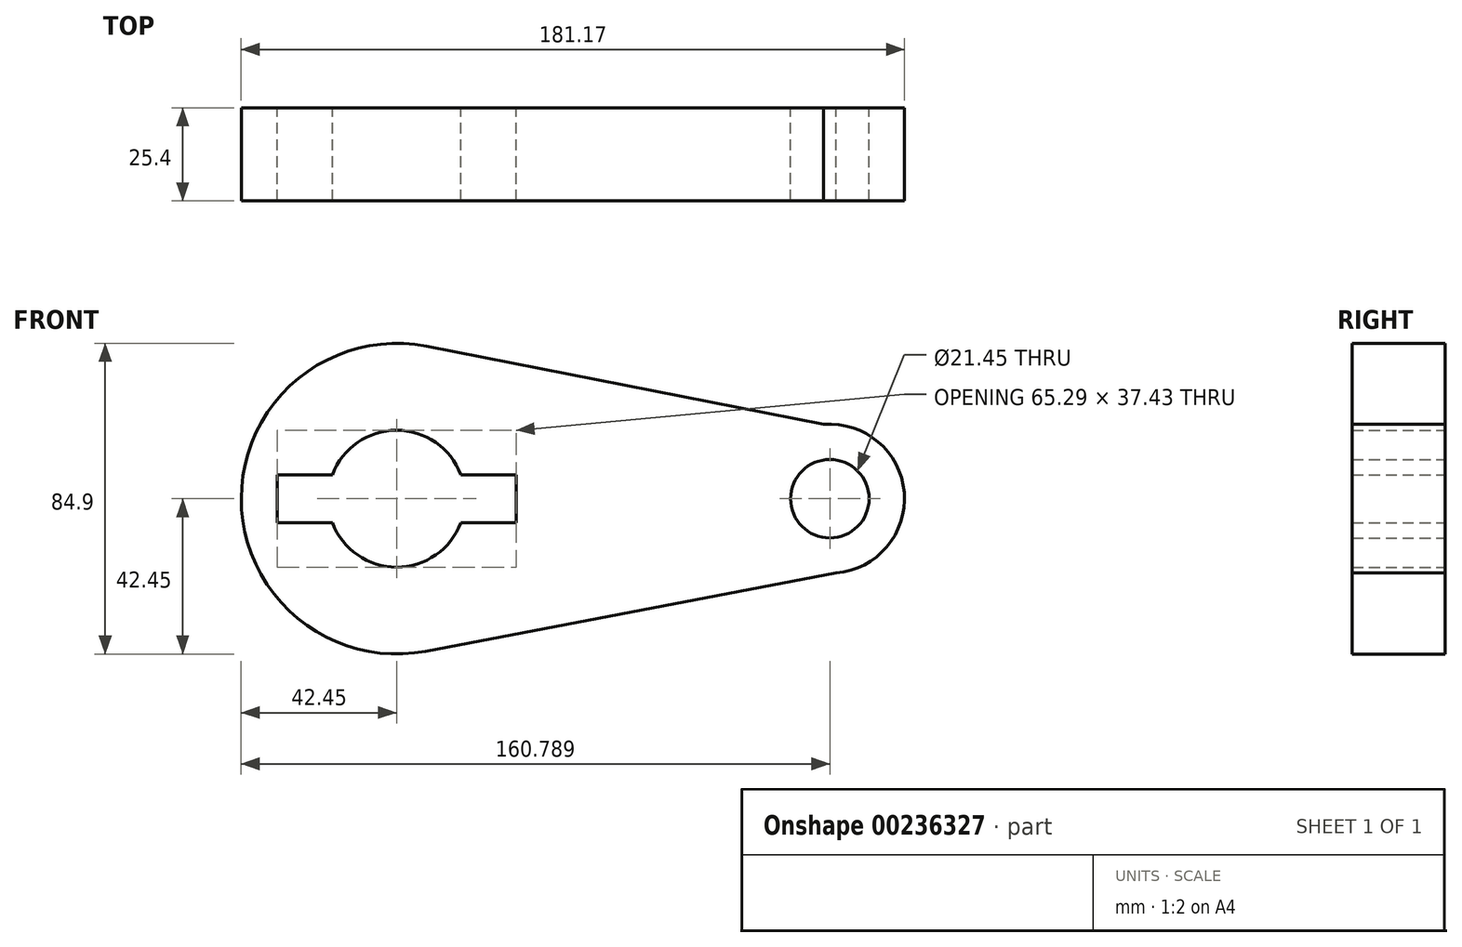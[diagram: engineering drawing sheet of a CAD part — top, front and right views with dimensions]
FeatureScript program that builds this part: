
annotation { "Feature Type Name" : "Feature", "Feature Type Description" : "" }
export const myFeature = defineFeature(function(context is Context, id is Id, definition is map)
    precondition{}
    {
        {
            var Q0;
            Q0=qCreatedBy(makeId("Front.planeOp"),FACE);
            var sketch = newSketch(context, id + "F0", { "sketchPlane" : qUnion([Q0])});
            skCircle(sketch, "E0", {"center": v(0, 0) * mm, "radius": 42.45 * mm});
            skCircle(sketch, "E1", {"center": v(118.34, 0) * mm, "radius": 20.38 * mm});
            skLineSegment(sketch, "E2", {"start": v(116.66, 20.3) * mm, "end": v(8.2, 41.65) * mm});
            skLineSegment(sketch, "E3", {"start": v(120.02, -20.3) * mm, "end": v(7.96, -41.7) * mm});
            skCircle(sketch, "E4", {"center": v(0, 0) * mm, "radius": 18.72 * mm});
            skCircle(sketch, "E5", {"center": v(118.34, 0) * mm, "radius": 10.73 * mm});
            skLineSegment(sketch, "E6.bottom", {"start": v(32.65, 6.56) * mm, "end": v(-32.65, 6.56) * mm});
            skLineSegment(sketch, "E6.top", {"start": v(32.65, -6.56) * mm, "end": v(-32.65, -6.56) * mm});
            skLineSegment(sketch, "E6.left", {"start": v(32.65, 6.56) * mm, "end": v(32.65, -6.56) * mm});
            skLineSegment(sketch, "E6.right", {"start": v(-32.65, 6.56) * mm, "end": v(-32.65, -6.56) * mm});
            skSolve(sketch);
        }
        {
            var Q0;
            Q0 = qSketchRegion(id + "F0", true);
            extrude(context, id + "F1", {"entities" : qUnion([Q0]), "depth" : 25.4 * mm});
        }
    });
